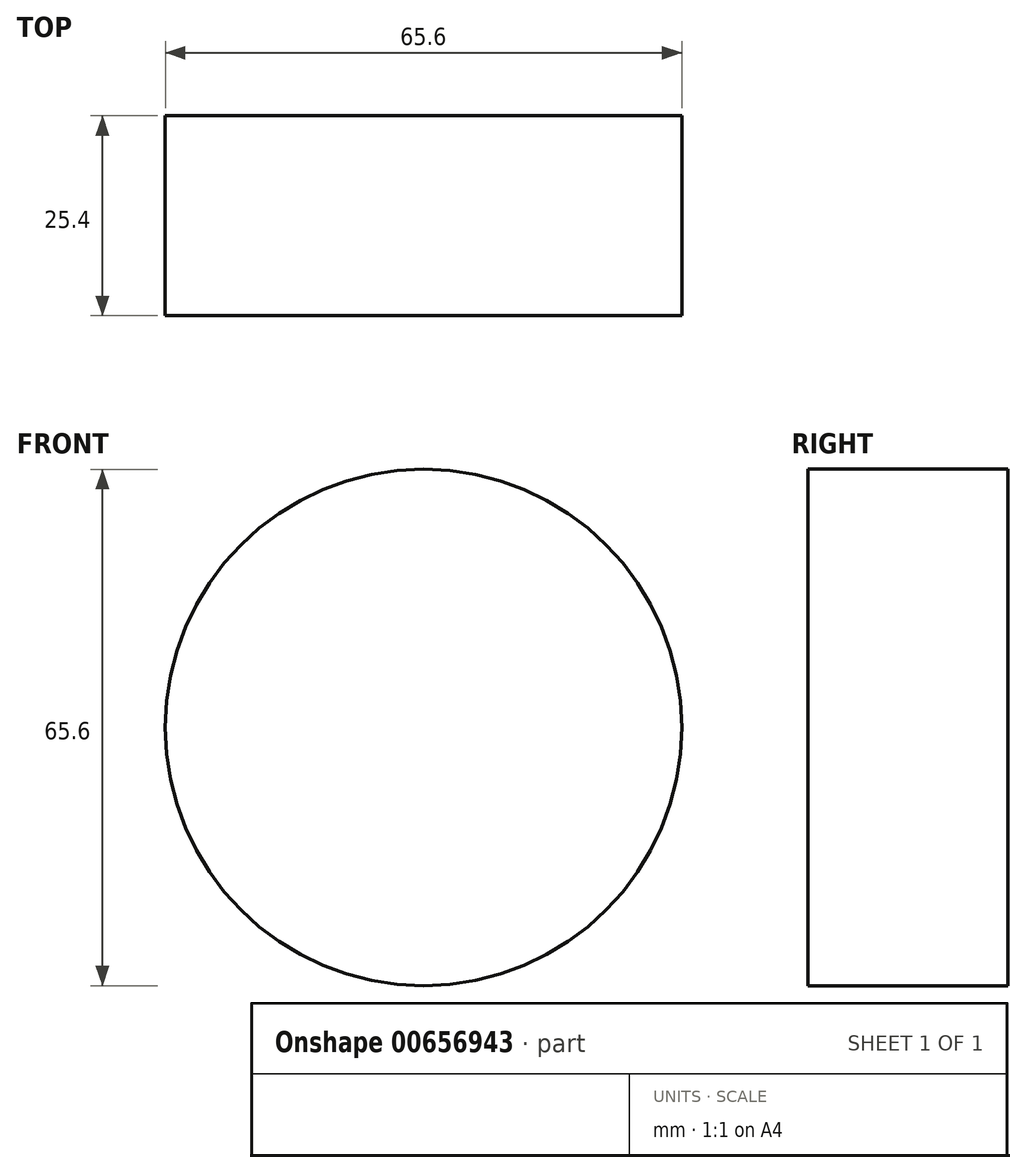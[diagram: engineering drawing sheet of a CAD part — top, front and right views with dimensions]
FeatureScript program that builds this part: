
annotation { "Feature Type Name" : "Feature", "Feature Type Description" : "" }
export const myFeature = defineFeature(function(context is Context, id is Id, definition is map)
    precondition{}
    {
        {
            var Q0;
            Q0=qCreatedBy(makeId("Front.planeOp"),FACE);
            var sketch = newSketch(context, id + "F0", { "sketchPlane" : qUnion([Q0])});
            skCircle(sketch, "E0", {"center": v(0, 0) * mm, "radius": 32.8 * mm});
            skSolve(sketch);
        }
        {
            var Q0;
            Q0 = qSketchRegion(id + "F0", true);
            extrude(context, id + "F1", {"entities" : qUnion([Q0]), "depth" : 25.4 * mm, "offsetDistance" : 25.4 * mm});
        }
    });
